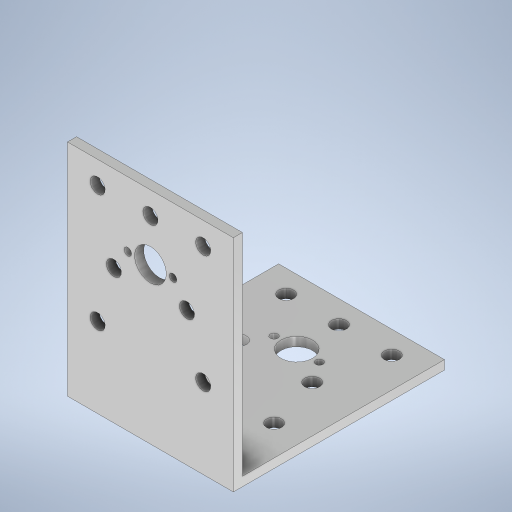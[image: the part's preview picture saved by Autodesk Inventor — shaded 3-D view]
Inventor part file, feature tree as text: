
AUTODESK INVENTOR PART (.ipt)
format: ipt  version: 2024 (Build 280153000, 153)  size: 302,080 bytes
history: native  units: in
note: dims shown in document units (in); Inventor stores cm internally (conversion verified against a paired STEP export)
features: sketch x8, hole x6, extrude x2, other x2, plane x1
ambient origin geometry x8: Origin, YZ Plane, XZ Plane, XY Plane, X Axis, Y Axis, Z Axis, Center Point
bodies: Solid1 (feature_tree)
feature tree (19):
  plane  "Work Plane1"
  extrude  "Extrusion1"  Depth=0.3937in
  extrude  "Extrusion2"  Depth=0.5512in
  hole  "Hole1"  [1 undecoded]
  hole  "Hole2"  [1 undecoded]
  hole  "Hole3"  [1 undecoded]
  sketch  "Sketch1"  dims[d5=2.7559in d6=0.0in]
  sketch  "Sketch2"  dims[d7=0.4134in d8=0.2953in d9=0.1476in d10=0.0984in d11=90.0deg d12=0.3937in d13=0.8108in]
  sketch  "Sketch3"  dims[d16=0.0984in d17=0.2953in d18=0.1476in d19=0.0984in d20=90.0deg d21=0.3937in d22=0.8108in]
  sketch  "Sketch4"  dims[d31=0.1969in d32=0.2953in d33=0.1476in d34=0.0984in d35=90.0deg d36=0.3937in d37=0.8108in d40=0.8465in]
  sketch  "Sketch5"  dims[d41=1.0827in d42=0.5512in]
  sketch  "Sketch6"  dims[d43=0.689in d44=0.689in]
  sketch  "Sketch7"  dims[d45=1.5354in d46=0.2953in]
  sketch  "Sketch8"  dims[d47=0.2953in d48=0.2953in d51=0.8108in d52=90.0deg d53=0.0984in d54=0.1476in d55=0.3937in d56=0.4134in d57=0.2953in d58=0.2953in d59=0.2953in d60=0.8108in d61=90.0deg d62=0.0984in d63=0.1476in d64=0.3937in d65=0.0984in d66=0.2953in d71=0.8108in d72=90.0deg d73=0.0984in d74=0.1476in d75=0.3937in d76=0.1969in d77=0.8465in d78=1.0827in d79=0.689in d80=0.689in d82=1.5354in d83=0.3937in d84=0.4134in d85=0.5512in]
  other  "Assembly1"
  other  "Base_Aluminum Plate:1"
  hole  "Hole6"  [1 undecoded]
  hole  "Hole4"  [1 undecoded]
  hole  "Hole5"  [1 undecoded]
note: 6 required parameter values undecoded (feature->parameter linkage not recoverable at this tier; creation-order binding heuristic only, values carry confidence <= 0.55)
